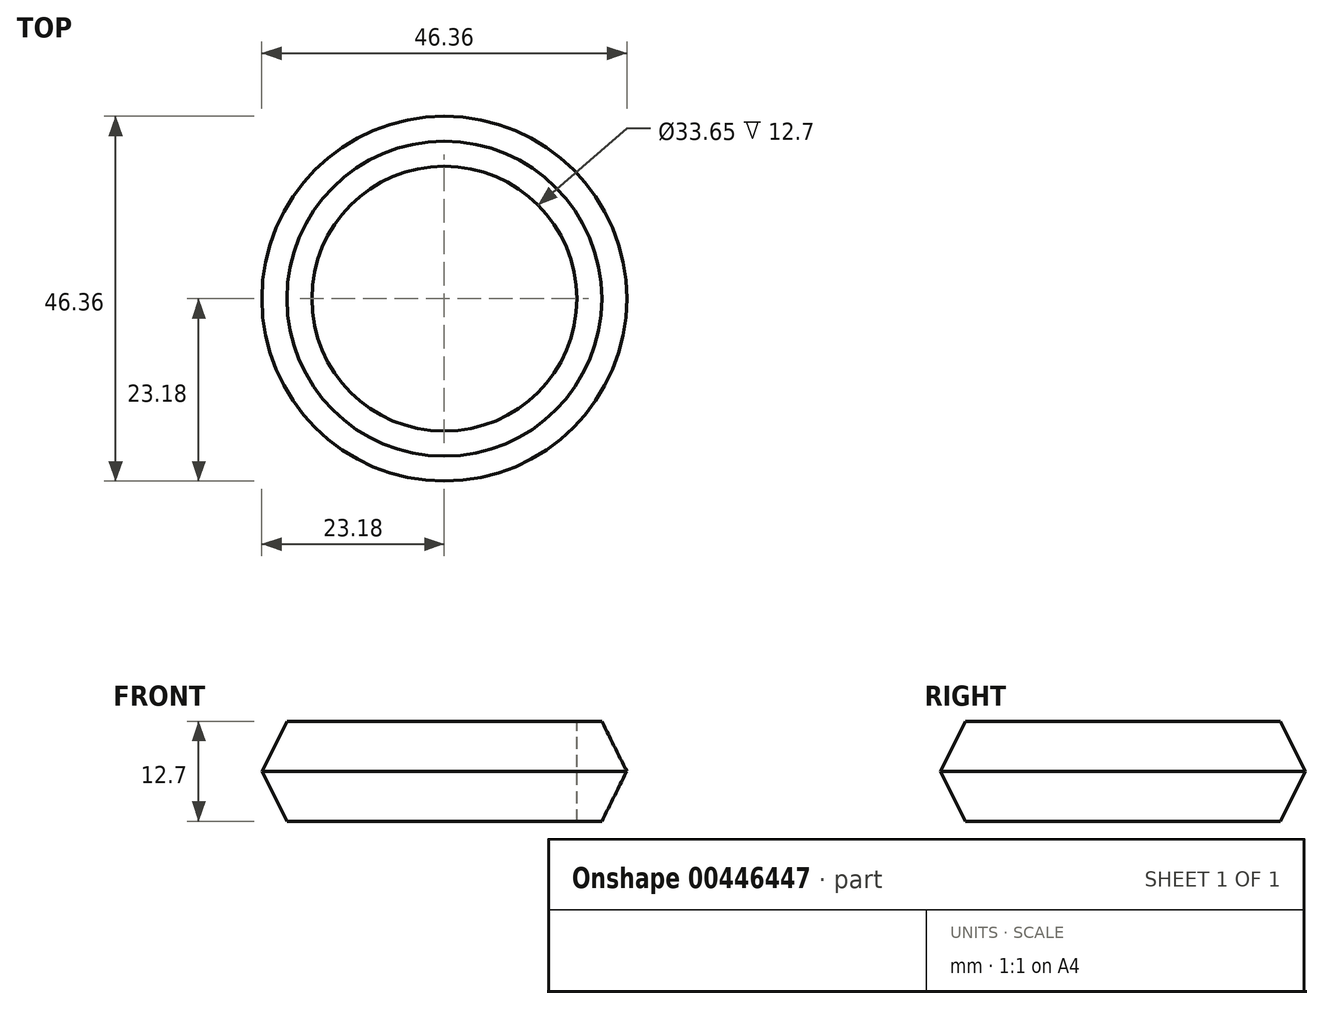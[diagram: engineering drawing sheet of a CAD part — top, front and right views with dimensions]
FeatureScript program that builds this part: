
annotation { "Feature Type Name" : "Feature", "Feature Type Description" : "" }
export const myFeature = defineFeature(function(context is Context, id is Id, definition is map)
    precondition{}
    {
        {
            var Q0;
            Q0=qCreatedBy(makeId("Top.planeOp"),FACE);
            var sketch = newSketch(context, id + "F0", { "sketchPlane" : qUnion([Q0])});
            skCircle(sketch, "E0", {"center": v(0, 0) * mm, "radius": 16.83 * mm});
            skCircle(sketch, "E1.0", {"center": v(0, 0) * mm, "radius": 20 * mm});
            skSolve(sketch);
        }
        {
            var Q0;
            Q0=makeQuery(id+"F0.imprint","IMPRINT",FACE,{"disambiguationData":[TD([[makeQuery(id+"F0.imprint","IMPRINT",EDGE,{"derivedFrom":sQuery(id+"F0.wireOp",EDGE,"E0")}),-1.0]])]});
            extrude(context, id + "F1", {"entities" : qUnion([Q0]), "depth" : 6.35 * mm, "offsetDistance" : 25.4 * mm});
        }
        {
            var Q0;
            Q0=qCreatedBy(makeId("Top.planeOp"),FACE);
            var sketch = newSketch(context, id + "F2", { "sketchPlane" : qUnion([Q0])});
            skCircle(sketch, "E2.0", {"center": v(0, 0) * mm, "radius": 23.18 * mm});
            skSolve(sketch);
        }
        {
            var Q0;
            Q0=makeQuery(id+"F1.opExtrude","CAP_FACE",FACE,{"disambiguationData":[OSD([sQuery(id+"F0.wireOp",EDGE,"E0"),sQuery(id+"F0.wireOp",EDGE,"E1.0")])],"isStart":false});
            var sketch = newSketch(context, id + "F3", { "sketchPlane" : qUnion([Q0])});
            skCircle(sketch, "E3.0", {"center": v(0, 0) * mm, "radius": 20 * mm});
            skSolve(sketch);
        }
        {
            var Q1;
            Q1 = qSketchRegion(id + "F3", true);
            var Q2;
            Q2 = qSketchRegion(id + "F2", true);
            loft(context, id + "F4", {"operationType" : NewBodyOperationType.ADD, "sheetProfilesArray" : [{ "sheetProfileEntities" : qUnion([Q1]) }, { "sheetProfileEntities" : qUnion([Q2]) }]});
        }
        {
            var Q0;
            Q0=makeQuery(id+"F1.opExtrude","SWEPT_BODY",BODY,{"disambiguationData":[OSD([sQuery(id+"F0.wireOp",EDGE,"E0"),sQuery(id+"F0.wireOp",EDGE,"E1.0")])]});
            var Q1;
            Q1=qCreatedBy(makeId("Top.planeOp"),FACE);
            mirror(context, id + "F5", {"operationType" : NewBodyOperationType.ADD, "entities" : qUnion([Q0]), "mirrorPlane" : qUnion([Q1])});
        }
        {
            var Q0;
            {var subQ0=sQuery(id+"F0.wireOp",EDGE,"E0");Q0=makeQuery(id+"F4.boolean.opBoolean","MERGE",FACE,{"derivedFrom":[makeQuery(id+"F1.opExtrude","CAP_FACE",FACE,{"disambiguationData":[OSD([subQ0,sQuery(id+"F0.wireOp",EDGE,"E1.0")])],"isStart":false}),makeQuery(id+"F4.opLoft","CAP_FACE",FACE,{"disambiguationData":[OSD([makeQuery(id+"F3.imprint","IMPRINT",FACE,{"disambiguationData":[TD([[makeQuery(id+"F3.imprint","IMPRINT",EDGE,{"derivedFrom":makeQuery(id+"F1.opExtrude","CAP_EDGE",EDGE,{"disambiguationData":[OSD([subQ0])],"isStart":false})}),1.0]])]})])],"isStart":true})]});}
            var sketch = newSketch(context, id + "F6", { "sketchPlane" : qUnion([Q0])});
            skCircle(sketch, "E4", {"center": v(0, 0) * mm, "radius": 16.83 * mm});
            skSolve(sketch);
        }
        {
            var Q0;
            Q0=makeQuery(id+"F6.imprint","IMPRINT",FACE,{"disambiguationData":[TD([[makeQuery(id+"F6.imprint","IMPRINT",EDGE,{"derivedFrom":sQuery(id+"F6.wireOp",EDGE,"E4")}),1.0]])]});
            extrude(context, id + "F7", {"entities" : qUnion([Q0]), "operationType" : NewBodyOperationType.REMOVE, "endBound" : BoundingType.THROUGH_ALL, "oppositeDirection" : true, "depth" : 25.4 * mm, "offsetDistance" : 25.4 * mm});
        }
    });
